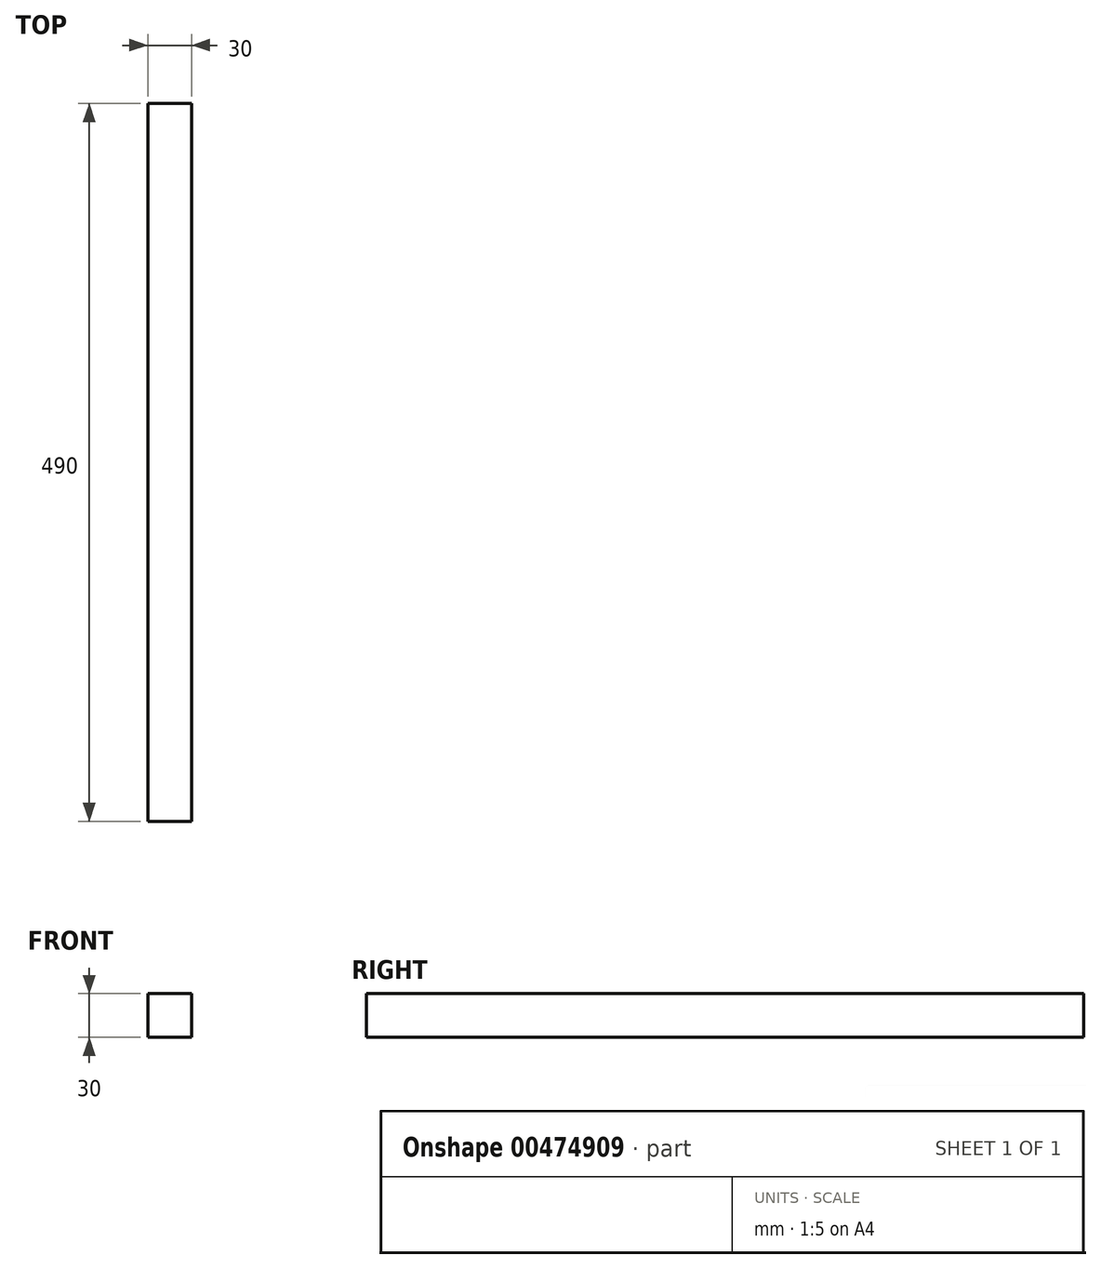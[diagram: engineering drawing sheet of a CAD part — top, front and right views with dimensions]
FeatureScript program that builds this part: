
annotation { "Feature Type Name" : "Feature", "Feature Type Description" : "" }
export const myFeature = defineFeature(function(context is Context, id is Id, definition is map)
    precondition{}
    {
        {
            var Q0;
            Q0=qCreatedBy(makeId("Right.planeOp"),FACE);
            var sketch = newSketch(context, id + "F0", { "sketchPlane" : qUnion([Q0])});
            skLineSegment(sketch, "E0.bottom", {"start": v(-59.04, -188.45) * mm, "end": v(430.96, -188.45) * mm});
            skLineSegment(sketch, "E0.top", {"start": v(-59.04, -218.45) * mm, "end": v(430.96, -218.45) * mm});
            skLineSegment(sketch, "E0.left", {"start": v(-59.04, -188.45) * mm, "end": v(-59.04, -218.45) * mm});
            skLineSegment(sketch, "E0.right", {"start": v(430.96, -188.45) * mm, "end": v(430.96, -218.45) * mm});
            skSolve(sketch);
        }
        {
            var Q0;
            Q0=qSketchRegion(id+"F0",true);
            extrude(context, id + "F1", {"entities" : qUnion([Q0]), "depth" : 30 * mm});
        }
    });
